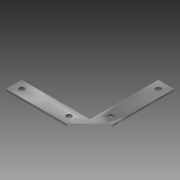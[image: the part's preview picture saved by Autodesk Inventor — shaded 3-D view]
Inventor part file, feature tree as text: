
AUTODESK INVENTOR PART (.ipt)
format: ipt  version: 2015 SP1 (Build 190203100, 203)  size: 118,784 bytes
history: native  units: in
note: dims shown in document units (in); Inventor stores cm internally (conversion verified against a paired STEP export)
features: sketch x2, extrude x1, hole x1
ambient origin geometry x8: Origin, YZ Plane, XZ Plane, XY Plane, X Axis, Y Axis, Z Axis, Center Point
bodies: Solid1 (feature_tree)
feature tree (4):
  extrude  "Extrusion1"  Depth=0.75in
  hole  "Hole1"  [1 undecoded]
  sketch  "Sketch1"  dims[d0=4.0in d1=0.75in]
  sketch  "Sketch2"  dims[d2=0.75in d3=4.0in d4=0.09in d5=0.0in d8=0.375in d11=0.375in d13=0.375in d14=0.375in d16=0.25in d17=0.75in d18=0.375in d19=0.25in d20=0.5635in d21=1.0in d22=0.8108in d23=1.375in d24=3.625in d25=1.375in d26=3.625in]
note: 1 required parameter value undecoded (feature->parameter linkage not recoverable at this tier; creation-order binding heuristic only, values carry confidence <= 0.55)
